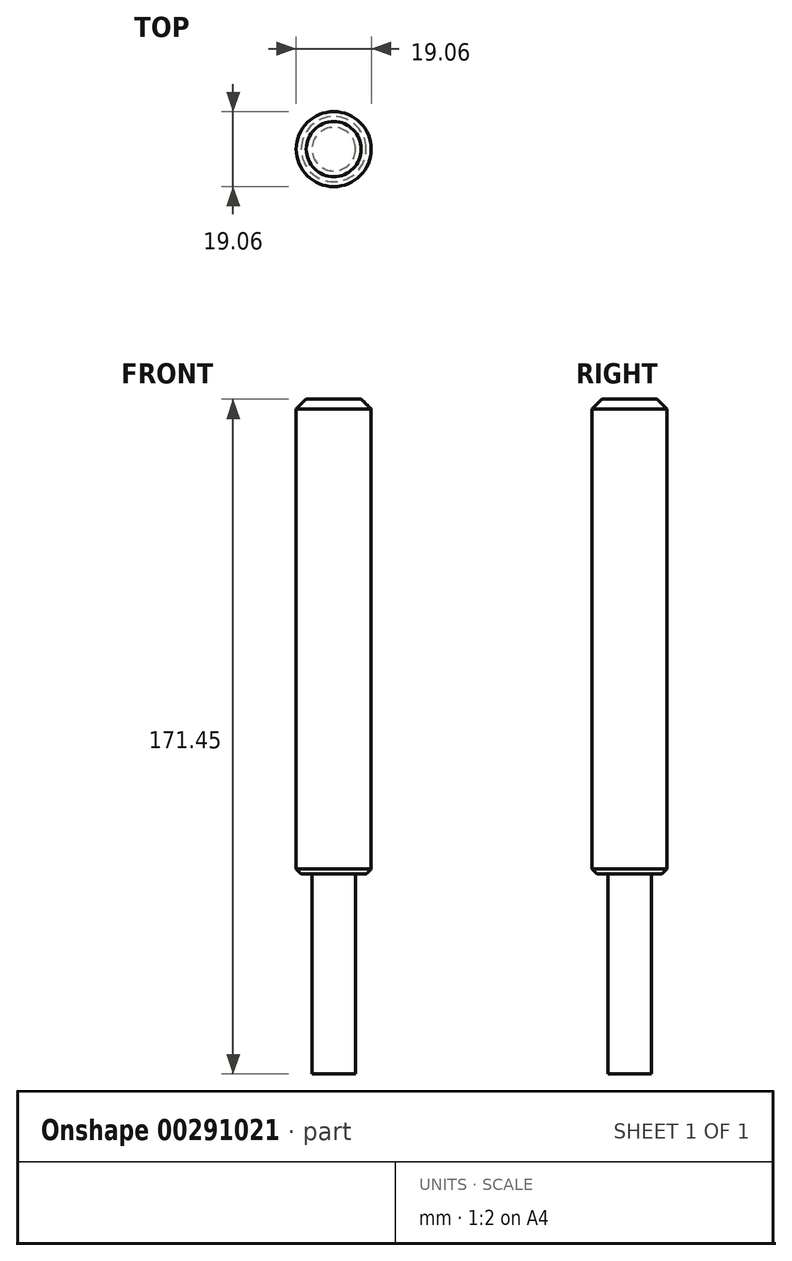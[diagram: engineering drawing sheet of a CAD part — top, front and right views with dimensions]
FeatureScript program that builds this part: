
annotation { "Feature Type Name" : "Feature", "Feature Type Description" : "" }
export const myFeature = defineFeature(function(context is Context, id is Id, definition is map)
    precondition{}
    {
        {
            var Q0;
            Q0=qCreatedBy(makeId("Top.planeOp"),FACE);
            var sketch = newSketch(context, id + "F0", { "sketchPlane" : qUnion([Q0])});
            skCircle(sketch, "E0", {"center": v(0, 0) * mm, "radius": 5.54 * mm});
            skSolve(sketch);
        }
        {
            var Q0;
            Q0=makeQuery(id+"F0.imprint","IMPRINT",FACE,{"disambiguationData":[TD([[makeQuery(id+"F0.imprint","IMPRINT",EDGE,{"derivedFrom":sQuery(id+"F0.wireOp",EDGE,"E0")}),1.0]])]});
            extrude(context, id + "F1", {"entities" : qUnion([Q0]), "depth" : 50.8 * mm});
        }
        {
            var Q0;
            Q0=makeQuery(id+"F1.opExtrude","CAP_FACE",FACE,{"disambiguationData":[OSD([sQuery(id+"F0.wireOp",EDGE,"E0")])],"isStart":false});
            var sketch = newSketch(context, id + "F2", { "sketchPlane" : qUnion([Q0])});
            skCircle(sketch, "E1", {"center": v(0, 0) * mm, "radius": 9.53 * mm});
            skSolve(sketch);
        }
        {
            var Q0;
            Q0 = qSketchRegion(id + "F2", true);
            extrude(context, id + "F3", {"entities" : qUnion([Q0]), "operationType" : NewBodyOperationType.ADD, "depth" : 120.65 * mm});
        }
        {
            var Q0;
            Q0=makeQuery(id+"F3.opExtrude","CAP_EDGE",EDGE,{"disambiguationData":[OSD([sQuery(id+"F2.wireOp",EDGE,"E1")])],"isStart":false});
            chamfer(context, id + "F4", {"entities" : qUnion([Q0]), "width" : 2.54 * mm, "tangentPropagation" : true});
        }
        {
            var Q0;
            Q0=makeQuery(id+"F3.opExtrude","CAP_EDGE",EDGE,{"disambiguationData":[OSD([sQuery(id+"F2.wireOp",EDGE,"E1")])],"isStart":true});
            chamfer(context, id + "F5", {"entities" : qUnion([Q0]), "width" : 1.27 * mm, "tangentPropagation" : true});
        }
    });
